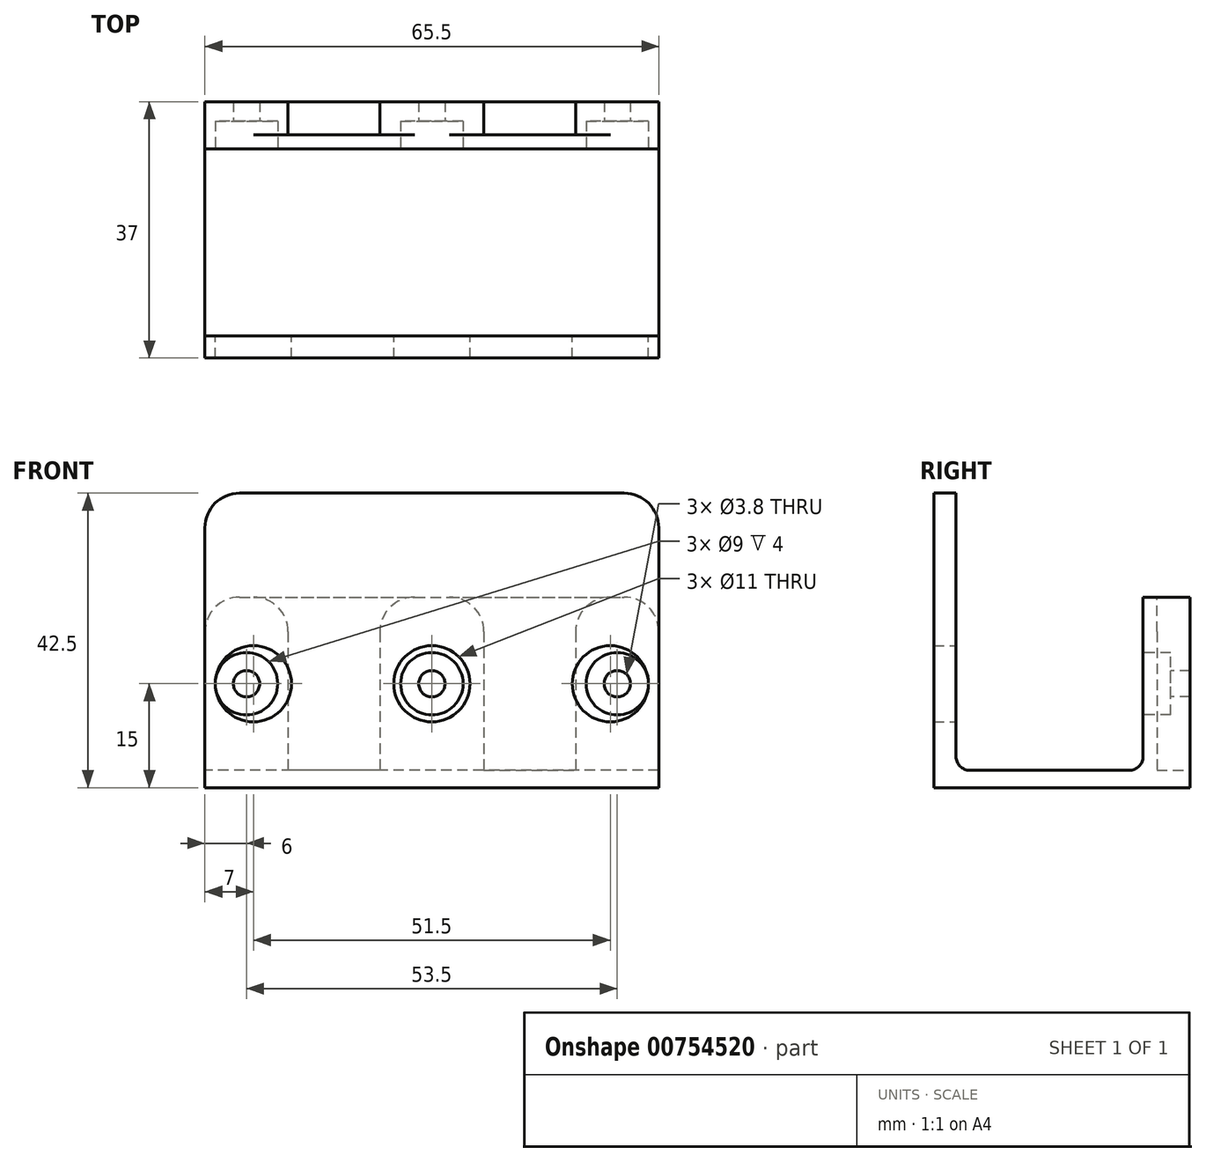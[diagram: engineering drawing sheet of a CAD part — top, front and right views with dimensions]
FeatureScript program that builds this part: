
annotation { "Feature Type Name" : "Feature", "Feature Type Description" : "" }
export const myFeature = defineFeature(function(context is Context, id is Id, definition is map)
    precondition{}
    {
        {
            var Q0;
            Q0=qCreatedBy(makeId("Top.planeOp"),FACE);
            var sketch = newSketch(context, id + "F0", { "sketchPlane" : qUnion([Q0])});
            skLineSegment(sketch, "E0.bottom", {"start": v(-32.75, 18.5) * mm, "end": v(32.75, 18.5) * mm});
            skLineSegment(sketch, "E0.top", {"start": v(-32.75, -18.5) * mm, "end": v(32.75, -18.5) * mm});
            skLineSegment(sketch, "E0.left", {"start": v(-32.75, 18.5) * mm, "end": v(-32.75, -18.5) * mm});
            skLineSegment(sketch, "E0.right", {"start": v(32.75, 18.5) * mm, "end": v(32.75, -18.5) * mm});
            skLineSegment(sketch, "E1", {"start": v(-32.75, 11.7) * mm, "end": v(32.75, 11.7) * mm});
            skLineSegment(sketch, "E2", {"start": v(-32.75, -15.3) * mm, "end": v(32.75, -15.3) * mm});
            skLineSegment(sketch, "E3", {"start": v(-20.75, 18.5) * mm, "end": v(-20.75, 13.7) * mm});
            skLineSegment(sketch, "E4", {"start": v(20.75, 13.7) * mm, "end": v(20.75, 18.5) * mm});
            skLineSegment(sketch, "E5", {"start": v(-7.5, 18.5) * mm, "end": v(-7.5, 13.7) * mm});
            skLineSegment(sketch, "E6", {"start": v(7.5, 18.5) * mm, "end": v(7.5, 13.7) * mm});
            skLineSegment(sketch, "E7", {"start": v(-20.75, 13.7) * mm, "end": v(-7.5, 13.7) * mm});
            skLineSegment(sketch, "E8", {"start": v(7.5, 13.7) * mm, "end": v(20.75, 13.7) * mm});
            skSolve(sketch);
        }
        {
            var Q0;
            Q0 = qSketchRegion(id + "F0", true);
            extrude(context, id + "F1", {"entities" : qUnion([Q0]), "depth" : 2.5 * mm, "offsetDistance" : 25 * mm});
        }
        {
            var Q0;
            {var subQ0=sQuery(id+"F0.wireOp",EDGE,"E0.bottom");Q0=makeQuery(id+"F0.imprint","IMPRINT",FACE,{"disambiguationData":[TD([[makeQuery(id+"F0.imprint","IMPRINT",EDGE,{"derivedFrom":subQ0}),-1.0]])]});}
            extrude(context, id + "F2", {"entities" : qUnion([Q0]), "operationType" : NewBodyOperationType.ADD, "depth" : 27.5 * mm, "offsetDistance" : 25 * mm});
        }
        {
            var Q0;
            {var subQ0=sQuery(id+"F0.wireOp",EDGE,"E0.top");Q0=makeQuery(id+"F0.imprint","IMPRINT",FACE,{"disambiguationData":[TD([[makeQuery(id+"F0.imprint","IMPRINT",EDGE,{"derivedFrom":subQ0}),1.0]])]});}
            extrude(context, id + "F3", {"entities" : qUnion([Q0]), "operationType" : NewBodyOperationType.ADD, "depth" : 42.5 * mm, "offsetDistance" : 25 * mm});
        }
        {
            var Q0;
            Q0=makeQuery(id+"F2.opExtrude","SWEPT_FACE",FACE,{"disambiguationData":[OSD([sQuery(id+"F0.wireOp",EDGE,"E1")])]});
            var sketch = newSketch(context, id + "F4", { "sketchPlane" : qUnion([Q0])});
            skCircle(sketch, "E9", {"center": v(-26.75, 15) * mm, "radius": 4.5 * mm});
            skCircle(sketch, "E10", {"center": v(0, 15) * mm, "radius": 4.5 * mm});
            skCircle(sketch, "E11", {"center": v(26.75, 15) * mm, "radius": 4.5 * mm});
            skLineSegment(sketch, "E12.0", {"start": v(-20.75, 27.5) * mm, "end": v(-20.75, 2.5) * mm, "construction": true});
            skLineSegment(sketch, "E13", {"start": v(-32.75, 15) * mm, "end": v(32.75, 15) * mm, "construction": true});
            skLineSegment(sketch, "E14", {"start": v(-20.75, 15) * mm, "end": v(-32.75, 15) * mm, "construction": true});
            skCircle(sketch, "E15", {"center": v(-26.75, 15) * mm, "radius": 1.9 * mm});
            skCircle(sketch, "E16", {"center": v(0, 15) * mm, "radius": 1.9 * mm});
            skCircle(sketch, "E17", {"center": v(26.75, 15) * mm, "radius": 1.9 * mm});
            skCircle(sketch, "E18", {"center": v(-25.75, 15) * mm, "radius": 5.5 * mm});
            skCircle(sketch, "E19", {"center": v(0, 15) * mm, "radius": 5.5 * mm});
            skCircle(sketch, "E20", {"center": v(25.75, 15) * mm, "radius": 5.5 * mm});
            skSolve(sketch);
        }
        {
            var Q0;
            Q0=makeQuery(id+"F4.imprint","IMPRINT",FACE,{"disambiguationData":[TD([[makeQuery(id+"F4.imprint","IMPRINT",EDGE,{"derivedFrom":sQuery(id+"F4.wireOp",EDGE,"E15")}),1.0]])]});
            var Q1;
            Q1=makeQuery(id+"F4.imprint","IMPRINT",FACE,{"disambiguationData":[TD([[makeQuery(id+"F4.imprint","IMPRINT",EDGE,{"derivedFrom":sQuery(id+"F4.wireOp",EDGE,"E16")}),1.0]])]});
            var Q2;
            Q2=makeQuery(id+"F4.imprint","IMPRINT",FACE,{"disambiguationData":[TD([[makeQuery(id+"F4.imprint","IMPRINT",EDGE,{"derivedFrom":sQuery(id+"F4.wireOp",EDGE,"E17")}),1.0]])]});
            extrude(context, id + "F5", {"entities" : qUnion([Q0, Q1, Q2]), "operationType" : NewBodyOperationType.REMOVE, "endBound" : BoundingType.THROUGH_ALL, "oppositeDirection" : true, "depth" : 25 * mm, "offsetDistance" : 25 * mm});
        }
        {
            var Q0;
            Q0=makeQuery(id+"F4.imprint","IMPRINT",FACE,{"disambiguationData":[TD([[makeQuery(id+"F4.imprint","IMPRINT",EDGE,{"derivedFrom":sQuery(id+"F4.wireOp",EDGE,"E9")}),1.0]])]});
            var Q1;
            Q1=makeQuery(id+"F4.imprint","IMPRINT",FACE,{"disambiguationData":[TD([[makeQuery(id+"F4.imprint","IMPRINT",EDGE,{"derivedFrom":sQuery(id+"F4.wireOp",EDGE,"E11")}),1.0]])]});
            var Q2;
            Q2=makeQuery(id+"F4.imprint","IMPRINT",FACE,{"disambiguationData":[TD([[makeQuery(id+"F4.imprint","IMPRINT",EDGE,{"derivedFrom":sQuery(id+"F4.wireOp",EDGE,"E10")}),1.0]])]});
            extrude(context, id + "F6", {"entities" : qUnion([Q0, Q1, Q2]), "operationType" : NewBodyOperationType.REMOVE, "oppositeDirection" : true, "depth" : 4 * mm, "offsetDistance" : 25 * mm});
        }
        {
            var Q0;
            Q0=makeQuery(id+"F4.imprint","IMPRINT",FACE,{"disambiguationData":[TD([[makeQuery(id+"F4.imprint","IMPRINT",EDGE,{"derivedFrom":sQuery(id+"F4.wireOp",EDGE,"E11")}),-1.0]])]});
            var Q1;
            Q1=makeQuery(id+"F4.imprint","IMPRINT",FACE,{"disambiguationData":[TD([[makeQuery(id+"F4.imprint","IMPRINT",EDGE,{"derivedFrom":sQuery(id+"F4.wireOp",EDGE,"E11")}),1.0]])]});
            var Q2;
            Q2=makeQuery(id+"F4.imprint","IMPRINT",FACE,{"disambiguationData":[TD([[makeQuery(id+"F4.imprint","IMPRINT",EDGE,{"derivedFrom":sQuery(id+"F4.wireOp",EDGE,"E17")}),1.0]])]});
            var Q3;
            Q3=makeQuery(id+"F4.imprint","IMPRINT",FACE,{"disambiguationData":[TD([[makeQuery(id+"F4.imprint","IMPRINT",EDGE,{"derivedFrom":sQuery(id+"F4.wireOp",EDGE,"E16")}),1.0]])]});
            var Q4;
            Q4=makeQuery(id+"F4.imprint","IMPRINT",FACE,{"disambiguationData":[TD([[makeQuery(id+"F4.imprint","IMPRINT",EDGE,{"derivedFrom":sQuery(id+"F4.wireOp",EDGE,"E10")}),1.0]])]});
            var Q5;
            Q5=makeQuery(id+"F4.imprint","IMPRINT",FACE,{"disambiguationData":[TD([[makeQuery(id+"F4.imprint","IMPRINT",EDGE,{"derivedFrom":sQuery(id+"F4.wireOp",EDGE,"E10")}),-1.0]])]});
            var Q6;
            Q6=makeQuery(id+"F4.imprint","IMPRINT",FACE,{"disambiguationData":[TD([[makeQuery(id+"F4.imprint","IMPRINT",EDGE,{"derivedFrom":sQuery(id+"F4.wireOp",EDGE,"E15")}),1.0]])]});
            var Q7;
            Q7=makeQuery(id+"F4.imprint","IMPRINT",FACE,{"disambiguationData":[TD([[makeQuery(id+"F4.imprint","IMPRINT",EDGE,{"derivedFrom":sQuery(id+"F4.wireOp",EDGE,"E9")}),1.0]])]});
            var Q8;
            Q8=makeQuery(id+"F4.imprint","IMPRINT",FACE,{"disambiguationData":[TD([[makeQuery(id+"F4.imprint","IMPRINT",EDGE,{"derivedFrom":sQuery(id+"F4.wireOp",EDGE,"E9")}),-1.0]])]});
            extrude(context, id + "F7", {"entities" : qUnion([Q0, Q1, Q2, Q3, Q4, Q5, Q6, Q7, Q8]), "operationType" : NewBodyOperationType.REMOVE, "endBound" : BoundingType.THROUGH_ALL, "depth" : 25 * mm, "offsetDistance" : 25 * mm});
        }
        {
            var Q0;
            Q0=makeQuery(id+"F2.opExtrude","CAP_EDGE",EDGE,{"disambiguationData":[OSD([sQuery(id+"F0.wireOp",EDGE,"E0.left")])],"isStart":false});
            var Q1;
            Q1=makeQuery(id+"F2.opExtrude","CAP_EDGE",EDGE,{"disambiguationData":[OSD([sQuery(id+"F0.wireOp",EDGE,"E0.right")])],"isStart":false});
            var Q2;
            Q2=makeQuery(id+"F2.opExtrude","CAP_EDGE",EDGE,{"disambiguationData":[OSD([sQuery(id+"F0.wireOp",EDGE,"E4")])],"isStart":false});
            var Q3;
            Q3=makeQuery(id+"F2.opExtrude","CAP_EDGE",EDGE,{"disambiguationData":[OSD([sQuery(id+"F0.wireOp",EDGE,"E6")])],"isStart":false});
            var Q4;
            Q4=makeQuery(id+"F2.opExtrude","CAP_EDGE",EDGE,{"disambiguationData":[OSD([sQuery(id+"F0.wireOp",EDGE,"E5")])],"isStart":false});
            var Q5;
            Q5=makeQuery(id+"F2.opExtrude","CAP_EDGE",EDGE,{"disambiguationData":[OSD([sQuery(id+"F0.wireOp",EDGE,"E3")])],"isStart":false});
            var Q6;
            Q6=makeQuery(id+"F3.opExtrude","CAP_EDGE",EDGE,{"disambiguationData":[OSD([sQuery(id+"F0.wireOp",EDGE,"E0.right")])],"isStart":false});
            var Q7;
            Q7=makeQuery(id+"F3.opExtrude","CAP_EDGE",EDGE,{"disambiguationData":[OSD([sQuery(id+"F0.wireOp",EDGE,"E0.left")])],"isStart":false});
            fillet(context, id + "F8", {"entities" : qUnion([Q0, Q1, Q2, Q3, Q4, Q5, Q6, Q7]), "radius" : 5 * mm, "tangentPropagation" : true, "allowEdgeOverflow" : false});
        }
        {
            var Q0;
            {var subQ0=sQuery(id+"F0.wireOp",EDGE,"E0.left");var subQ1=sQuery(id+"F0.wireOp",EDGE,"E0.right");var subQ2=sQuery(id+"F0.wireOp",EDGE,"E0.top");Q0=makeQuery(id+"F3.boolean.opBoolean","INTERSECT",EDGE,{"derivedFrom":[makeQuery(id+"F2.boolean.opBoolean","SPLIT",FACE,{"disambiguationData":[TD([makeQuery(id+"F1.opExtrude","SWEPT_FACE",FACE,{"disambiguationData":[OSD([subQ2])]})])],"derivedFrom":makeQuery(id+"F1.opExtrude","CAP_FACE",FACE,{"disambiguationData":[OSD([sQuery(id+"F0.wireOp",EDGE,"E0.bottom"),subQ2,subQ0,subQ1])],"isStart":false})}),makeQuery(id+"F3.opExtrude","SWEPT_FACE",FACE,{"disambiguationData":[OSD([sQuery(id+"F0.wireOp",EDGE,"E2")])]})]});}
            var Q1;
            Q1=makeQuery(id+"F2.boolean.opBoolean","INTERSECT",EDGE,{"derivedFrom":[makeQuery(id+"F1.opExtrude","CAP_FACE",FACE,{"disambiguationData":[OSD([sQuery(id+"F0.wireOp",EDGE,"E0.bottom"),sQuery(id+"F0.wireOp",EDGE,"E0.top"),sQuery(id+"F0.wireOp",EDGE,"E0.left"),sQuery(id+"F0.wireOp",EDGE,"E0.right")])],"isStart":false}),makeQuery(id+"F2.opExtrude","SWEPT_FACE",FACE,{"disambiguationData":[OSD([sQuery(id+"F0.wireOp",EDGE,"E1")])]})]});
            fillet(context, id + "F9", {"entities" : qUnion([Q0, Q1]), "radius" : 2 * mm, "tangentPropagation" : true, "allowEdgeOverflow" : false});
        }
    });
